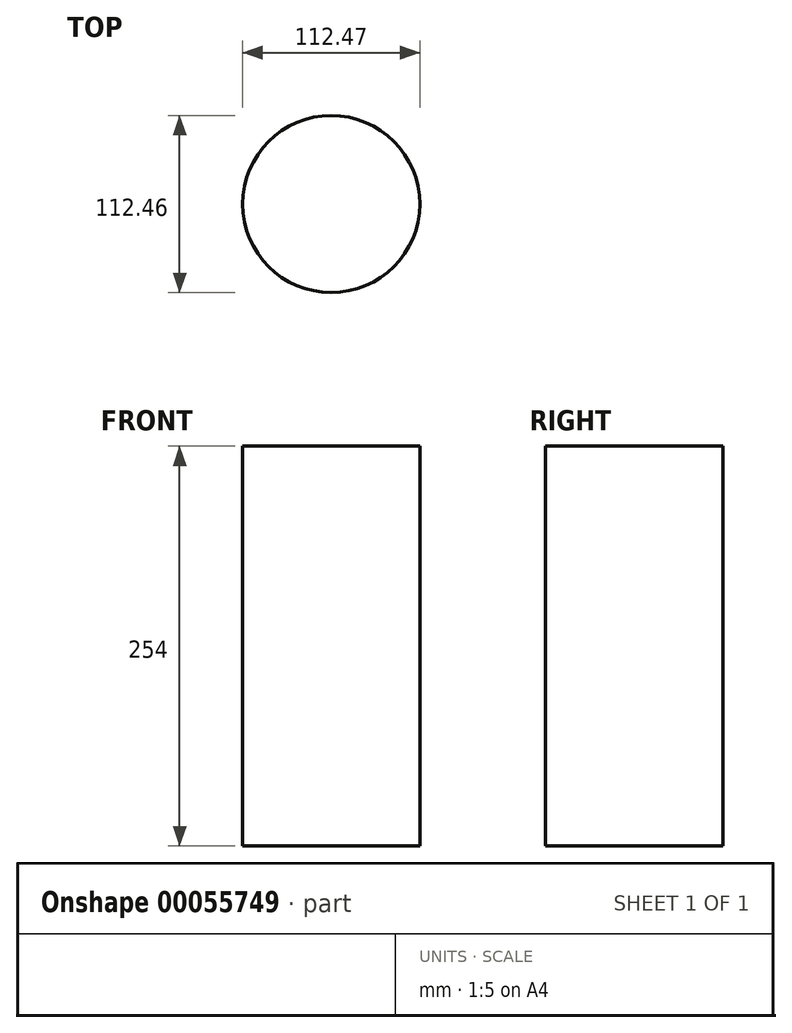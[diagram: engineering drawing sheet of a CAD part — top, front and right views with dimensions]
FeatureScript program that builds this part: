
annotation { "Feature Type Name" : "Feature", "Feature Type Description" : "" }
export const myFeature = defineFeature(function(context is Context, id is Id, definition is map)
    precondition{}
    {
        {
            var Q0;
            Q0=qCreatedBy(makeId("Top.planeOp"),FACE);
            var sketch = newSketch(context, id + "F0", { "sketchPlane" : qUnion([Q0])});
            skCircle(sketch, "E0", {"center": v(-16.4, 10.33) * mm, "radius": 56.23 * mm});
            skSolve(sketch);
        }
        {
            var Q0;
            Q0=makeQuery(id+"F0.imprint","IMPRINT",FACE,{"disambiguationData":[TD([[makeQuery(id+"F0.imprint","IMPRINT",EDGE,{"derivedFrom":sQuery(id+"F0.wireOp",EDGE,"E0")}),1.0]])]});
            extrude(context, id + "F1", {"entities" : qUnion([Q0]), "depth" : 254 * mm});
        }
    });
